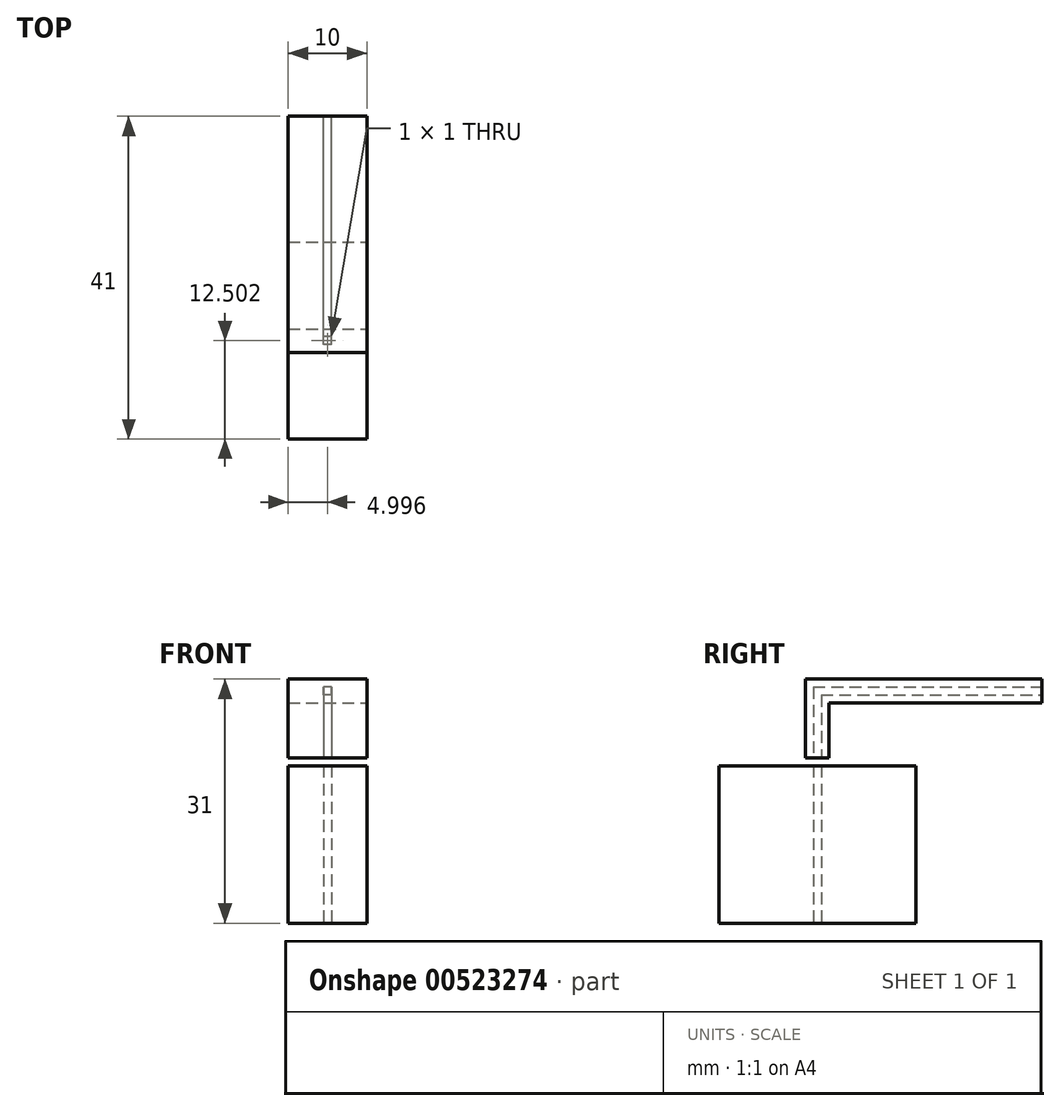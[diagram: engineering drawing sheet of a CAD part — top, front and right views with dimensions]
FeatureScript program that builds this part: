
annotation { "Feature Type Name" : "Feature", "Feature Type Description" : "" }
export const myFeature = defineFeature(function(context is Context, id is Id, definition is map)
    precondition{}
    {
        {
            var Q0;
            Q0=qCreatedBy(makeId("Top.planeOp"),FACE);
            var sketch = newSketch(context, id + "F0", { "sketchPlane" : qUnion([Q0])});
            skLineSegment(sketch, "E0.bottom", {"start": v(-21.4, 15.87) * mm, "end": v(-11.4, 15.87) * mm});
            skLineSegment(sketch, "E0.top", {"start": v(-21.4, -9.13) * mm, "end": v(-11.4, -9.13) * mm});
            skLineSegment(sketch, "E0.left", {"start": v(-21.4, 15.87) * mm, "end": v(-21.4, -9.13) * mm});
            skLineSegment(sketch, "E0.right", {"start": v(-11.4, 15.87) * mm, "end": v(-11.4, -9.13) * mm});
            skLineSegment(sketch, "E1.bottom", {"start": v(-16.9, 3.87) * mm, "end": v(-15.9, 3.87) * mm});
            skLineSegment(sketch, "E1.top", {"start": v(-16.9, 2.87) * mm, "end": v(-15.9, 2.87) * mm});
            skLineSegment(sketch, "E1.left", {"start": v(-16.9, 3.87) * mm, "end": v(-16.9, 2.87) * mm});
            skLineSegment(sketch, "E1.right", {"start": v(-15.9, 3.87) * mm, "end": v(-15.9, 2.87) * mm});
            skSolve(sketch);
        }
        {
            var Q0;
            Q0=makeQuery(id+"F0.imprint","IMPRINT",FACE,{"disambiguationData":[TD([[makeQuery(id+"F0.imprint","IMPRINT",EDGE,{"derivedFrom":sQuery(id+"F0.wireOp",EDGE,"E0.bottom")}),-1.0]])]});
            extrude(context, id + "F1", {"entities" : qUnion([Q0]), "depth" : 20 * mm, "offsetDistance" : 25 * mm});
        }
        {
            var Q0;
            Q0=makeQuery(id+"F1.opExtrude","SWEPT_FACE",FACE,{"disambiguationData":[OSD([sQuery(id+"F0.wireOp",EDGE,"E0.right")])]});
            var sketch = newSketch(context, id + "F2", { "sketchPlane" : qUnion([Q0])});
            skLineSegment(sketch, "E2.bottom", {"start": v(1.87, 21) * mm, "end": v(4.87, 21) * mm});
            skLineSegment(sketch, "E2.top", {"start": v(1.87, 31) * mm, "end": v(4.87, 31) * mm});
            skLineSegment(sketch, "E2.left", {"start": v(4.87, 21) * mm, "end": v(4.87, 31) * mm});
            skLineSegment(sketch, "E2.right", {"start": v(1.87, 21) * mm, "end": v(1.87, 31) * mm});
            skLineSegment(sketch, "E3.bottom", {"start": v(4.87, 31) * mm, "end": v(31.87, 31) * mm});
            skLineSegment(sketch, "E3.top", {"start": v(4.87, 28) * mm, "end": v(31.87, 28) * mm});
            skLineSegment(sketch, "E3.left", {"start": v(4.87, 31) * mm, "end": v(4.87, 28) * mm});
            skLineSegment(sketch, "E3.right", {"start": v(31.87, 31) * mm, "end": v(31.87, 28) * mm});
            skSolve(sketch);
        }
        {
            var Q0;
            Q0=makeQuery(id+"F2.imprint","IMPRINT",FACE,{"disambiguationData":[TD([[makeQuery(id+"F2.imprint","IMPRINT",EDGE,{"derivedFrom":sQuery(id+"F2.wireOp",EDGE,"E2.bottom")}),1.0]])]});
            var Q1;
            Q1=makeQuery(id+"F2.imprint","IMPRINT",FACE,{"disambiguationData":[TD([[makeQuery(id+"F2.imprint","IMPRINT",EDGE,{"derivedFrom":sQuery(id+"F2.wireOp",EDGE,"E3.bottom")}),-1.0]])]});
            extrude(context, id + "F3", {"entities" : qUnion([Q0, Q1]), "oppositeDirection" : true, "depth" : 10 * mm, "offsetDistance" : 25 * mm});
        }
        {
            var Q0;
            Q0=makeQuery(id+"F3.opExtrude","SWEPT_FACE",FACE,{"disambiguationData":[OSD([sQuery(id+"F2.wireOp",EDGE,"E2.bottom")])]});
            var sketch = newSketch(context, id + "F4", { "sketchPlane" : qUnion([Q0])});
            skLineSegment(sketch, "E4.bottom", {"start": v(-15.9, -2.87) * mm, "end": v(-16.9, -2.87) * mm});
            skLineSegment(sketch, "E4.top", {"start": v(-15.9, -3.87) * mm, "end": v(-16.9, -3.87) * mm});
            skLineSegment(sketch, "E4.left", {"start": v(-15.9, -2.87) * mm, "end": v(-15.9, -3.87) * mm});
            skLineSegment(sketch, "E4.right", {"start": v(-16.9, -2.87) * mm, "end": v(-16.9, -3.87) * mm});
            skSolve(sketch);
        }
        {
            var Q0;
            Q0=makeQuery(id+"F4.imprint","IMPRINT",FACE,{"disambiguationData":[TD([[makeQuery(id+"F4.imprint","IMPRINT",EDGE,{"derivedFrom":sQuery(id+"F4.wireOp",EDGE,"E4.bottom")}),1.0]])]});
            extrude(context, id + "F5", {"entities" : qUnion([Q0]), "operationType" : NewBodyOperationType.REMOVE, "oppositeDirection" : true, "depth" : 9 * mm, "offsetDistance" : 25 * mm});
        }
        {
            var Q0;
            Q0=makeQuery(id+"F3.opExtrude","SWEPT_FACE",FACE,{"disambiguationData":[OSD([sQuery(id+"F2.wireOp",EDGE,"E3.right")])]});
            var sketch = newSketch(context, id + "F6", { "sketchPlane" : qUnion([Q0])});
            skLineSegment(sketch, "E5.bottom", {"start": v(15.9, 29) * mm, "end": v(16.9, 29) * mm});
            skLineSegment(sketch, "E5.top", {"start": v(15.9, 30) * mm, "end": v(16.9, 30) * mm});
            skLineSegment(sketch, "E5.left", {"start": v(15.9, 29) * mm, "end": v(15.9, 30) * mm});
            skLineSegment(sketch, "E5.right", {"start": v(16.9, 29) * mm, "end": v(16.9, 30) * mm});
            skSolve(sketch);
        }
        {
            var Q0;
            Q0=makeQuery(id+"F6.imprint","IMPRINT",FACE,{"disambiguationData":[TD([[makeQuery(id+"F6.imprint","IMPRINT",EDGE,{"derivedFrom":sQuery(id+"F6.wireOp",EDGE,"E5.bottom")}),1.0]])]});
            extrude(context, id + "F7", {"entities" : qUnion([Q0]), "operationType" : NewBodyOperationType.REMOVE, "oppositeDirection" : true, "depth" : 29 * mm, "offsetDistance" : 25 * mm});
        }
    });
